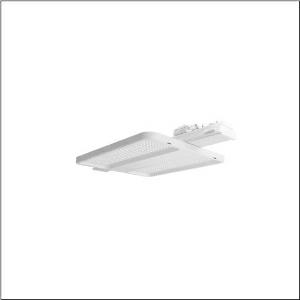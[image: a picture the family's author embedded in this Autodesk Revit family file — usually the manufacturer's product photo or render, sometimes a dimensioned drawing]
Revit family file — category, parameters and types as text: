
# Revit family: highbay_11_fur_licross_r__tragschiene_midi_51hn11da4mla_c1e5
name_source: partatom
category: Lighting Fixtures
units: mm (PartAtom-declared; Revit-internal decimal feet)

## family parameters
Cut with Voids When Loaded = No
Host = Face
Light Source = No
Part Type = Normal
Room Calculation Point = No
Round Connector Dimension = Use Diameter
Shared = No

## types (1)
- --- (1 x LED, 28000 lm, 146.6 W, 4000K)
    Apparent Load = 147 VA
    CIE Flux Codes = 85 97 100 100 100
    Color Rendering = 80
    Color Temperature = 4000K
    Default Elevation = 1800 mm
    Description = Highbay 11 for Licross® trunking rail midi, high bay luminaire, primary light control with lens, of PMMA, primary optical cover: cover, of PMMA, light emission: direct distribution, primary light characteristic: symmetric, LED, rated luminous flux: 28.000lm, luminous efficacy: 191lm/W, light colour: 840, colour temperature: 4000K, control gear: DALI 2, with plug, 5-pole, with phase selection, mains connection: 230..240V, AC, 50/60Hz, rated input power: 146.6W, housing frame, of high-performance plastic PA6, matt traffic white (RAL 9016), length: 750mm, width: 442mm, height: 71mm, lever catch, fixing on rail side, of steel, galvanised, white, blank cover, of PC/ABS, traffic white (RAL 9016), protection rating (complete): IP64, insulation class (complete): insulation class I (protective earthing), certification: CE, ENEC, VDE, UKCA, protection symbol: D, impact resistance: IK07, permissible operating ambient temperature: -40..+50°C, corresponds to IFS (International Featured Standards) requirements for safety and quality in the food industry, LABS conformity tested according to VDMA 24364:2018-05, packaging unit: 1 piece
    Height = 72 mm  [stored 0.23622 ft]
    Lamp = 1 x LED
    Lamp Light Flux = 28000 lm
    Lamp Power = 146.6 W
    Lamp count = 1
    Length = 474 mm
    Luminous efficacy = 191 lm/W
    Manufacturer = Siteco
    ModVariant = No
    Model = 51HN11DA4MLA
    Mounting Place = Ceiling
    Mounting Type = Pendant
    Number of Poles = 1
    OnlyDefault = Yes
    Power Factor = 1
    Product Name = Highbay 11 für Licross® Tragschiene midi
    Product group = high bay luminaire
    ProductGroupID = 901
    Protection Class = Protection class I
    Protection Degree = IP 64
    RLX_Detail_Level = 1
    RLX_Emergency_Light_Flux = 0 lm
    RLX_Emergency_Type = 0
    RLX_Emergency_Type_DB = No
    RlxData = <blob elided: 16969 chars, md5=7236ce63>
    Socket = socket
    Standby Power = 0 W
    System Light Flux = 28001 lm
    System Power = 147 W
    Type Comments = factory setting: luminous flux: 100 % | dim-lin: 254 | 661 mA
    Type Image = l_1363258.jpg
    URL = http://relux.com
    VarID = @adj_004949
    Voltage = 0 V
    Weight = 0.00 kg
    Width = 442 mm

note: [stored X ft] marks values corroborated as IEEE doubles in the binary element streams (Revit-internal decimal feet)

## geometry (parser evidence)
native form markers: Blend x4, Sweep x11
no freeform markers — native parametric forms only
